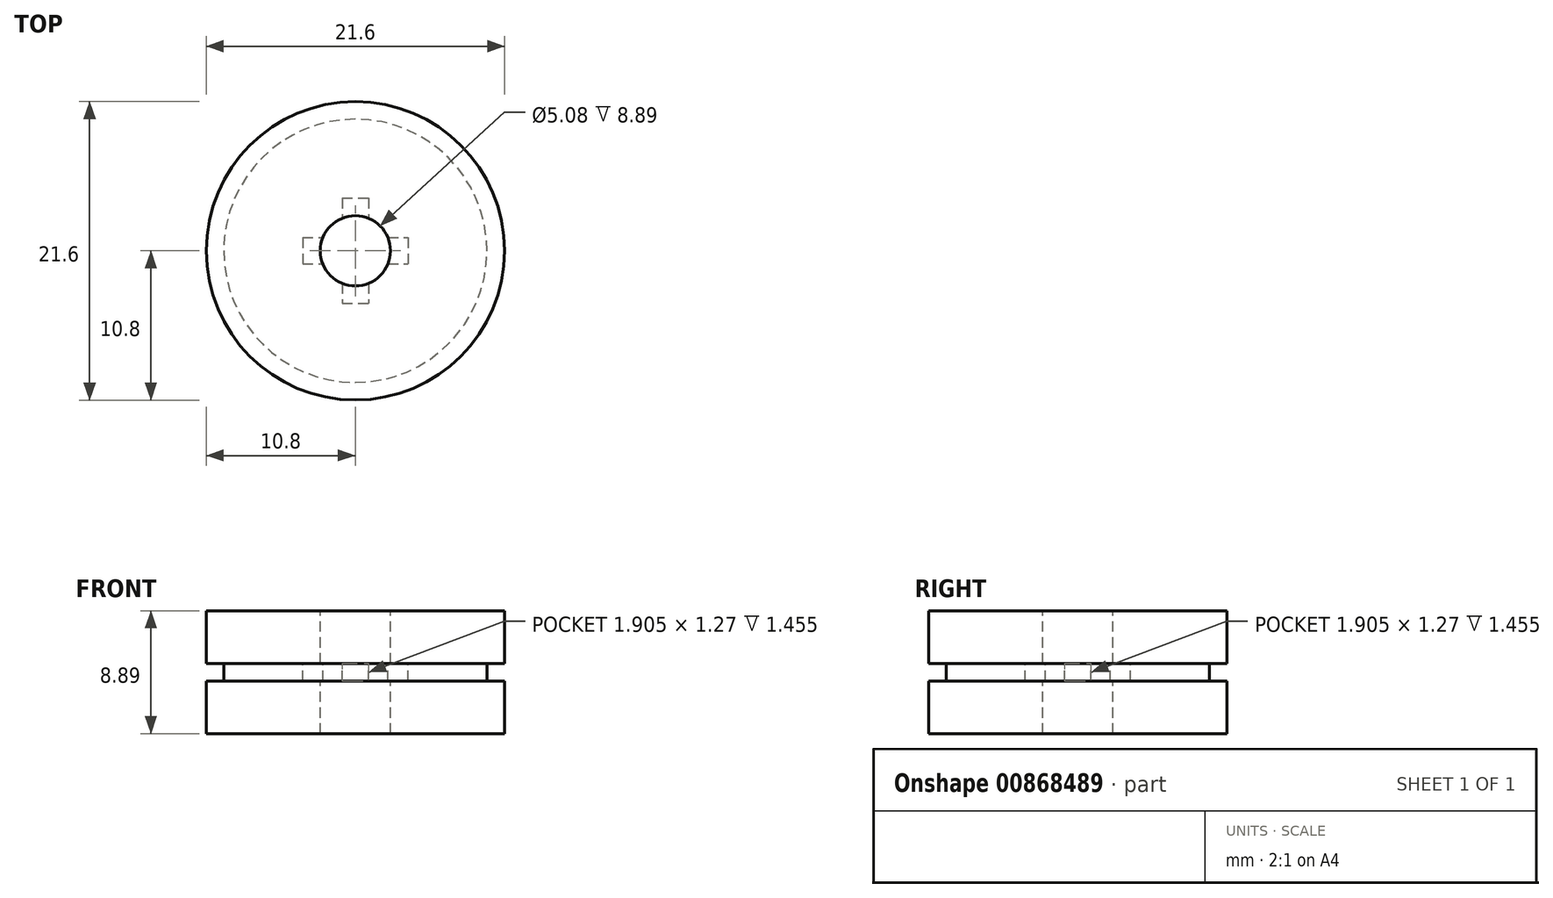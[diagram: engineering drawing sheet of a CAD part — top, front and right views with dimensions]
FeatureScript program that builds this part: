
annotation { "Feature Type Name" : "Feature", "Feature Type Description" : "" }
export const myFeature = defineFeature(function(context is Context, id is Id, definition is map)
    precondition{}
    {
        {
            var Q0;
            Q0=qCreatedBy(makeId("Top.planeOp"),FACE);
            var sketch = newSketch(context, id + "F0", { "sketchPlane" : qUnion([Q0])});
            skCircle(sketch, "E0", {"center": v(0, 0) * mm, "radius": 10.8 * mm});
            skSolve(sketch);
        }
        {
            var Q0;
            Q0 = qSketchRegion(id + "F0", true);
            extrude(context, id + "F1", {"entities" : qUnion([Q0]), "depth" : 8.9 * mm, "offsetDistance" : 25.4 * mm});
        }
        {
            var Q0;
            Q0=makeQuery(id+"F1.opExtrude","CAP_FACE",FACE,{"disambiguationData":[OSD([sQuery(id+"F0.wireOp",EDGE,"E0")])],"isStart":false});
            cPlane(context, id + "F2", {"entities" : qUnion([Q0]), "cplaneType" : CPlaneType.OFFSET, "offset" : 4.44 * mm, "oppositeDirection" : true, "width" : 152.4 * mm, "height" : 152.4 * mm});
        }
        {
            var Q0;
            Q0=qCreatedBy(id+"F2.planeOp",FACE);
            var sketch = newSketch(context, id + "F3", { "sketchPlane" : qUnion([Q0])});
            skCircle(sketch, "E1", {"center": v(0, 0) * mm, "radius": 9.53 * mm});
            skCircle(sketch, "E2", {"center": v(0, 0) * mm, "radius": 10.8 * mm});
            skSolve(sketch);
        }
        {
            var Q0;
            Q0 = qSketchRegion(id + "F3", true);
            extrude(context, id + "F4", {"entities" : qUnion([Q0]), "operationType" : NewBodyOperationType.REMOVE, "endBound" : BoundingType.SYMMETRIC, "depth" : 1.27 * mm, "offsetDistance" : 25.4 * mm});
        }
        {
            var Q0;
            Q0=makeQuery(id+"F1.opExtrude","CAP_FACE",FACE,{"disambiguationData":[OSD([sQuery(id+"F0.wireOp",EDGE,"E0")])],"isStart":false});
            var sketch = newSketch(context, id + "F5", { "sketchPlane" : qUnion([Q0])});
            skCircle(sketch, "E3", {"center": v(0, 0) * mm, "radius": 2.54 * mm});
            skSolve(sketch);
        }
        {
            var Q0;
            Q0 = qSketchRegion(id + "F5", true);
            extrude(context, id + "F6", {"entities" : qUnion([Q0]), "operationType" : NewBodyOperationType.REMOVE, "endBound" : BoundingType.THROUGH_ALL, "oppositeDirection" : true, "depth" : 25.4 * mm, "offsetDistance" : 25.4 * mm});
        }
        {
            var Q0;
            Q0=qCreatedBy(id+"F2.planeOp",FACE);
            var sketch = newSketch(context, id + "F7", { "sketchPlane" : qUnion([Q0])});
            skLineSegment(sketch, "E4.bottom", {"start": v(-0.95, 3.81) * mm, "end": v(0.95, 3.81) * mm});
            skLineSegment(sketch, "E4.top", {"start": v(-0.95, -3.81) * mm, "end": v(0.95, -3.81) * mm});
            skLineSegment(sketch, "E4.left", {"start": v(-0.95, 3.81) * mm, "end": v(-0.95, 0.95) * mm});
            skLineSegment(sketch, "E4.right", {"start": v(0.95, 3.81) * mm, "end": v(0.95, 0.95) * mm});
            skLineSegment(sketch, "E5.bottom", {"start": v(-3.81, 0.95) * mm, "end": v(-0.95, 0.95) * mm});
            skLineSegment(sketch, "E5.top", {"start": v(-3.81, -0.95) * mm, "end": v(-0.95, -0.95) * mm});
            skLineSegment(sketch, "E5.left", {"start": v(-3.81, 0.95) * mm, "end": v(-3.81, -0.95) * mm});
            skLineSegment(sketch, "E5.right", {"start": v(3.81, 0.95) * mm, "end": v(3.81, -0.95) * mm});
            skLineSegment(sketch, "E6.trimOffspring", {"start": v(-0.95, -0.95) * mm, "end": v(-0.95, -3.81) * mm});
            skLineSegment(sketch, "E7.trimOffspring", {"start": v(0.95, -0.95) * mm, "end": v(3.81, -0.95) * mm});
            skLineSegment(sketch, "E8.trimOffspring", {"start": v(0.95, -0.95) * mm, "end": v(0.95, -3.81) * mm});
            skLineSegment(sketch, "E9.trimOffspring", {"start": v(0.95, 0.95) * mm, "end": v(3.81, 0.95) * mm});
            skSolve(sketch);
        }
        {
            var Q0;
            Q0 = qSketchRegion(id + "F7", true);
            extrude(context, id + "F8", {"entities" : qUnion([Q0]), "operationType" : NewBodyOperationType.REMOVE, "endBound" : BoundingType.SYMMETRIC, "oppositeDirection" : true, "depth" : 1.27 * mm, "offsetDistance" : 25.4 * mm});
        }
    });
